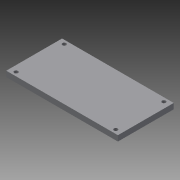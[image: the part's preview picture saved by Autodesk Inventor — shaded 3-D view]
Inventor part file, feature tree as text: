
AUTODESK INVENTOR PART (.ipt)
format: ipt  version: 2013 (Build 170138000, 138)  size: 81,408 bytes
history: native  units: mm
features: sketch x2, extrude x1, hole x1
ambient origin geometry x8: Origin, YZ Plane, XZ Plane, XY Plane, X Axis, Y Axis, Z Axis, Center Point
bodies: Solid1 (feature_tree)
feature tree (4):
  extrude  "Extrusion1"  Depth=101.6mm
  hole  "Hole1"  [1 undecoded]
  sketch  "Sketch1"  dims[d0=50.8mm d2=101.6mm]
  sketch  "Sketch2"  dims[d3=5.0mm d4=0.0mm d5=43.815mm d7=90.678mm d8=3.4mm d9=6.0mm d10=6.5mm d11=3.0mm d12=90.0deg d13=8.0mm d14=20.594885mm]
note: 1 required parameter value undecoded (feature->parameter linkage not recoverable at this tier; creation-order binding heuristic only, values carry confidence <= 0.55)
